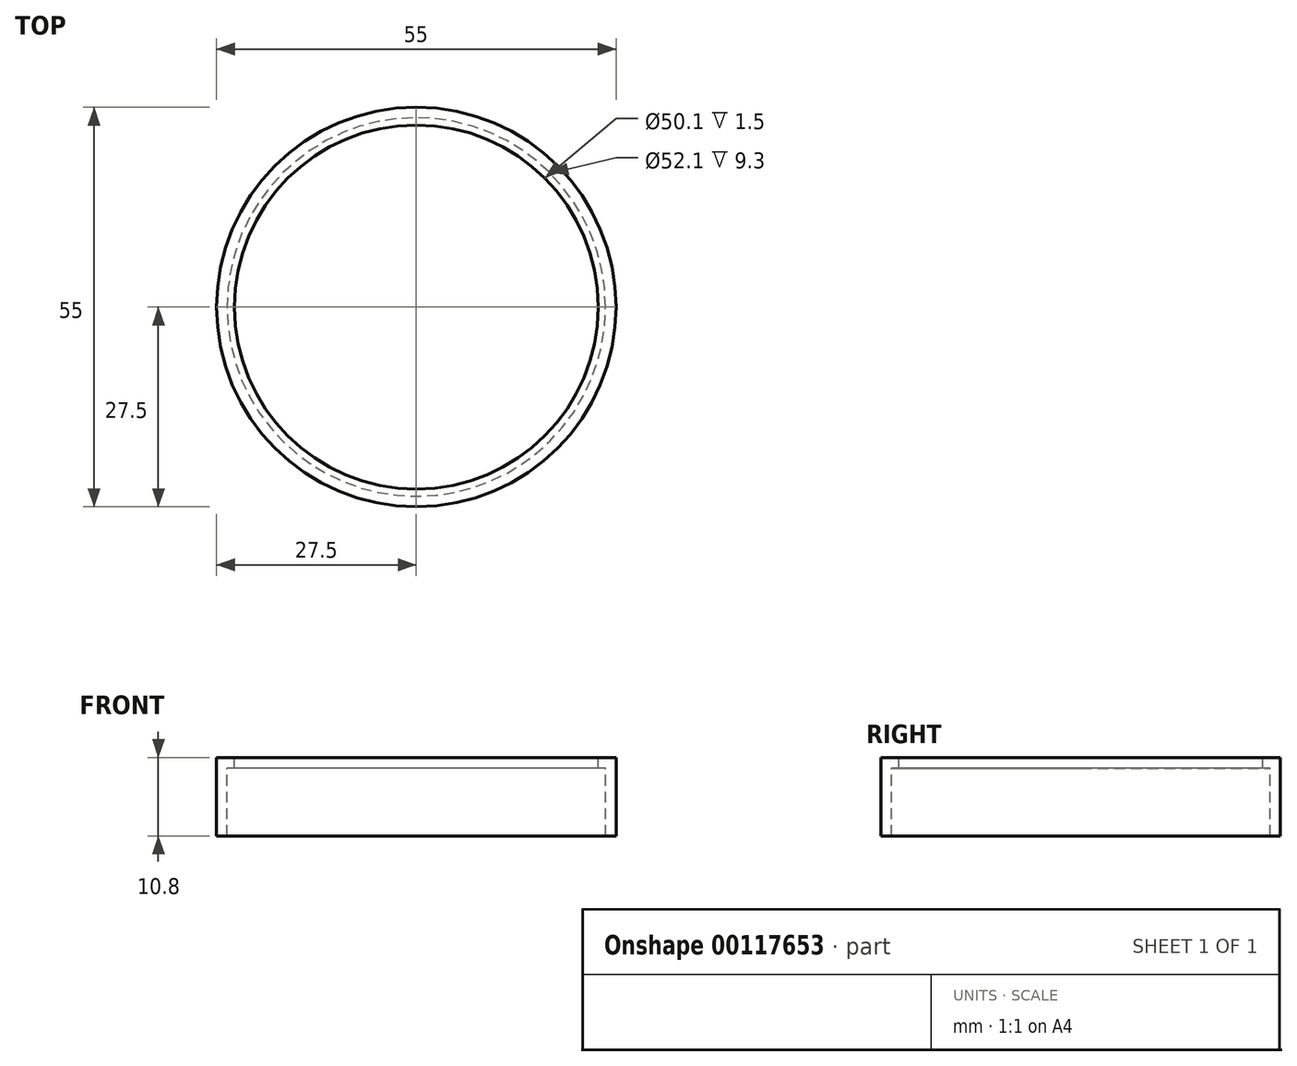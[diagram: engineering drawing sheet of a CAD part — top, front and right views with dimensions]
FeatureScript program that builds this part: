
annotation { "Feature Type Name" : "Feature", "Feature Type Description" : "" }
export const myFeature = defineFeature(function(context is Context, id is Id, definition is map)
    precondition{}
    {
        {
            var Q0;
            Q0=qCreatedBy(makeId("Front.planeOp"),FACE);
            var sketch = newSketch(context, id + "F0", { "sketchPlane" : qUnion([Q0])});
            skLineSegment(sketch, "E0", {"start": v(0, 4.56) * mm, "end": v(0, -3.27) * mm, "construction": true});
            skLineSegment(sketch, "E1.bottom", {"start": v(25.05, 0) * mm, "end": v(27.5, 0) * mm});
            skLineSegment(sketch, "E1.top", {"start": v(26.05, -10.8) * mm, "end": v(27.5, -10.8) * mm});
            skLineSegment(sketch, "E1.left", {"start": v(26.05, -1.5) * mm, "end": v(26.05, -10.8) * mm});
            skLineSegment(sketch, "E1.right", {"start": v(27.5, 0) * mm, "end": v(27.5, -10.8) * mm});
            skLineSegment(sketch, "E2", {"start": v(26.05, -1.5) * mm, "end": v(25.05, -1.5) * mm});
            skLineSegment(sketch, "E3", {"start": v(25.05, -1.5) * mm, "end": v(25.05, 0) * mm});
            skSolve(sketch);
        }
        {
            var Q0;
            Q0=makeQuery(id+"F0.imprint","IMPRINT",FACE,{"disambiguationData":[TD([[makeQuery(id+"F0.imprint","IMPRINT",EDGE,{"derivedFrom":sQuery(id+"F0.wireOp",EDGE,"E1.bottom")}),-1.0]])]});
            var Q1;
            Q1=sQuery(id+"F0.wireOp",EDGE,"E0");
            revolve(context, id + "F1", {"entities" : qUnion([Q0]), "axis" : qUnion([Q1]), "revolveType" : RevolveType.FULL});
        }
    });
